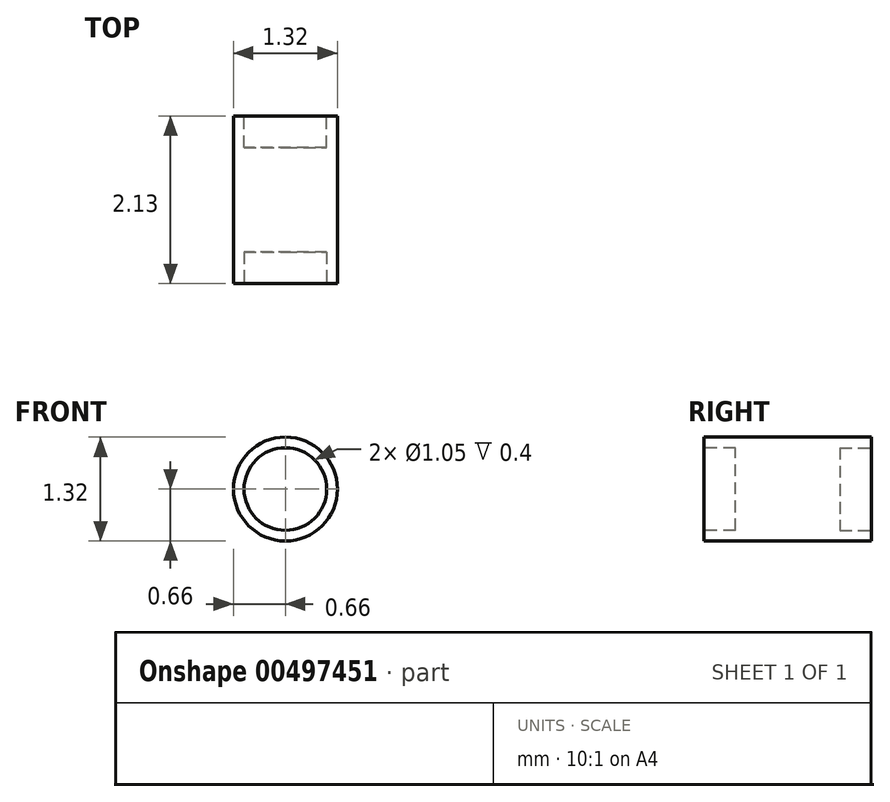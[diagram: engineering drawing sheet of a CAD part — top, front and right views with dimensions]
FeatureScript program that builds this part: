
annotation { "Feature Type Name" : "Feature", "Feature Type Description" : "" }
export const myFeature = defineFeature(function(context is Context, id is Id, definition is map)
    precondition{}
    {
        {
            var Q0;
            Q0=qCreatedBy(makeId("Front.planeOp"),FACE);
            var sketch = newSketch(context, id + "F0", { "sketchPlane" : qUnion([Q0])});
            skCircle(sketch, "E0", {"center": v(0, 0) * mm, "radius": 0.66 * mm});
            skSolve(sketch);
        }
        {
            var Q0;
            Q0 = qSketchRegion(id + "F0", true);
            extrude(context, id + "F1", {"entities" : qUnion([Q0]), "depth" : 2.13 * mm});
        }
        {
            var Q0;
            Q0=makeQuery(id+"F1.opExtrude","CAP_FACE",FACE,{"disambiguationData":[OSD([sQuery(id+"F0.wireOp",EDGE,"E0")])],"isStart":false});
            var sketch = newSketch(context, id + "F2", { "sketchPlane" : qUnion([Q0])});
            skCircle(sketch, "E1", {"center": v(0, 0) * mm, "radius": 0.53 * mm});
            skSolve(sketch);
        }
        {
            var Q0;
            Q0 = qSketchRegion(id + "F2", true);
            extrude(context, id + "F3", {"entities" : qUnion([Q0]), "operationType" : NewBodyOperationType.REMOVE, "oppositeDirection" : true, "depth" : .4 * mm});
        }
        {
            var Q0;
            Q0=makeQuery(id+"F1.opExtrude","CAP_FACE",FACE,{"disambiguationData":[OSD([sQuery(id+"F0.wireOp",EDGE,"E0")])],"isStart":true});
            var sketch = newSketch(context, id + "F4", { "sketchPlane" : qUnion([Q0])});
            skCircle(sketch, "E2", {"center": v(0, 0) * mm, "radius": 0.53 * mm});
            skSolve(sketch);
        }
        {
            var Q0;
            Q0 = qSketchRegion(id + "F4", true);
            extrude(context, id + "F5", {"entities" : qUnion([Q0]), "operationType" : NewBodyOperationType.REMOVE, "oppositeDirection" : true, "depth" : .4 * mm});
        }
    });
